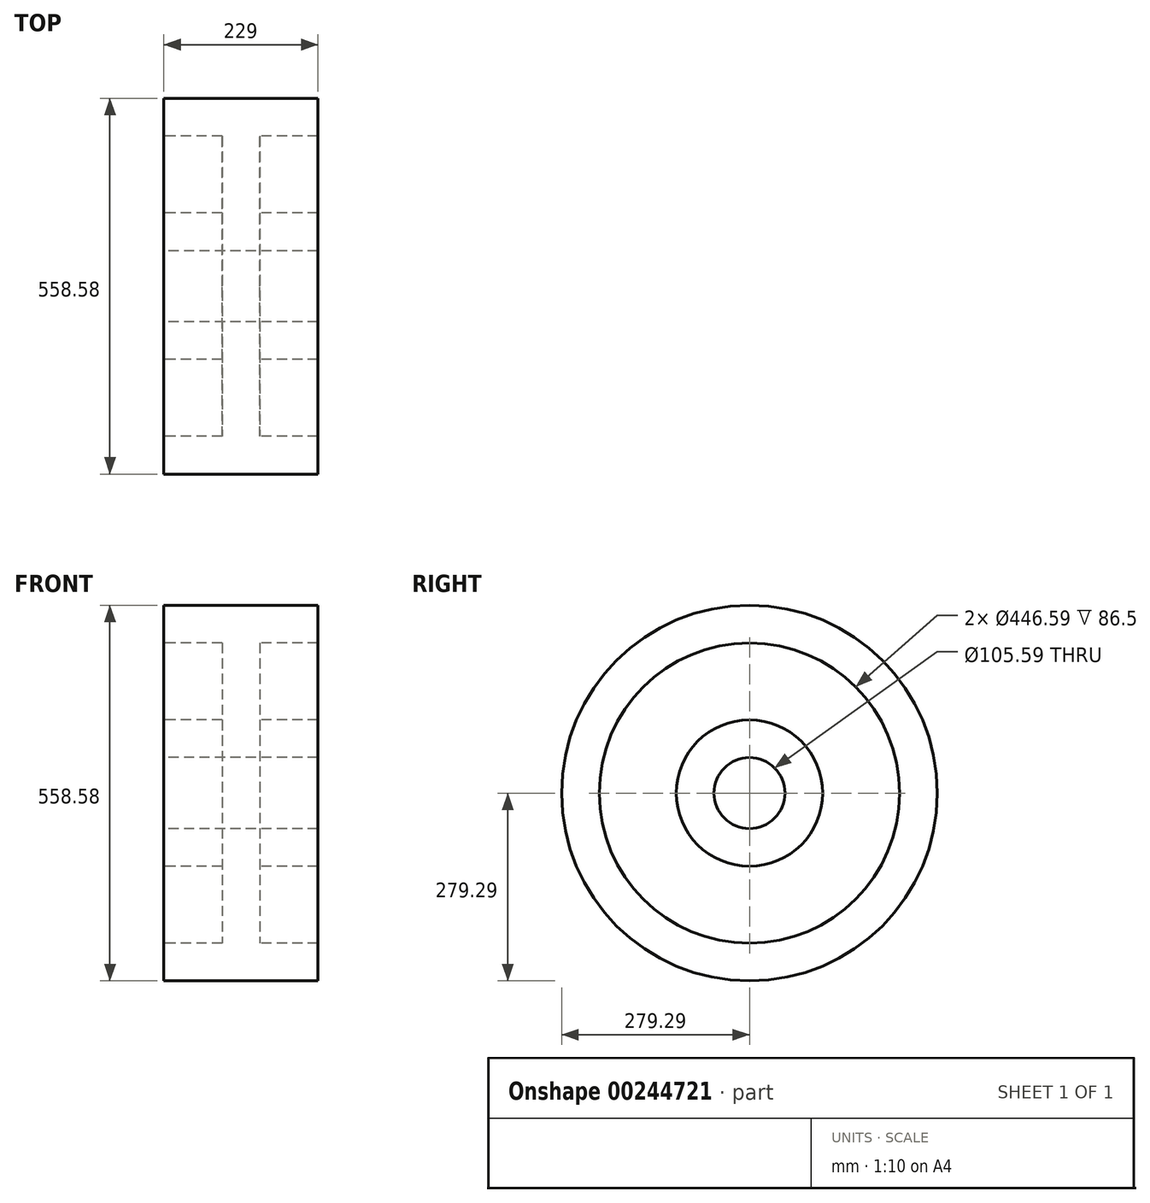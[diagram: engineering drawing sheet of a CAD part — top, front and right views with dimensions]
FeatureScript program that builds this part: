
annotation { "Feature Type Name" : "Feature", "Feature Type Description" : "" }
export const myFeature = defineFeature(function(context is Context, id is Id, definition is map)
    precondition{}
    {
        {
            var Q0;
            Q0=qCreatedBy(makeId("Front.planeOp"),FACE);
            var sketch = newSketch(context, id + "F0", { "sketchPlane" : qUnion([Q0])});
            skLineSegment(sketch, "E0", {"start": v(-122.5, 0) * mm, "end": v(122.5, 0) * mm, "construction": true});
            skLineSegment(sketch, "E1", {"start": v(-114.5, 279.3) * mm, "end": v(-114.5, 223.3) * mm});
            skLineSegment(sketch, "E2", {"start": v(-114.5, 279.3) * mm, "end": v(114.5, 279.3) * mm});
            skLineSegment(sketch, "E3", {"start": v(114.5, 279.3) * mm, "end": v(114.5, 223.3) * mm});
            skLineSegment(sketch, "E4", {"start": v(-114.5, 223.3) * mm, "end": v(-28, 223.3) * mm});
            skLineSegment(sketch, "E5", {"start": v(-28, 223.3) * mm, "end": v(-28, 108.8) * mm});
            skLineSegment(sketch, "E6", {"start": v(-28, 108.8) * mm, "end": v(-114.5, 108.8) * mm});
            skLineSegment(sketch, "E7", {"start": v(-114.5, 108.8) * mm, "end": v(-114.5, 52.8) * mm});
            skLineSegment(sketch, "E8", {"start": v(-114.5, 52.8) * mm, "end": v(114.5, 52.8) * mm});
            skLineSegment(sketch, "E9", {"start": v(114.5, 52.8) * mm, "end": v(114.5, 108.8) * mm});
            skLineSegment(sketch, "E10", {"start": v(28, 108.8) * mm, "end": v(28, 223.3) * mm});
            skLineSegment(sketch, "E11", {"start": v(28, 108.8) * mm, "end": v(114.5, 108.8) * mm});
            skLineSegment(sketch, "E12", {"start": v(28, 223.3) * mm, "end": v(114.5, 223.3) * mm});
            skLineSegment(sketch, "E13", {"start": v(0, 0) * mm, "end": v(0, 292.3) * mm, "construction": true});
            skPoint(sketch, "E13.endSnap0", {"position": v(0, 0) * mm});
            skSolve(sketch);
        }
        {
            var Q0;
            Q0 = qSketchRegion(id + "F0", true);
            var Q1;
            Q1=sQuery(id+"F0.wireOp",EDGE,"E0");
            revolve(context, id + "F1", {"entities" : qUnion([Q0]), "axis" : qUnion([Q1]), "revolveType" : RevolveType.FULL});
        }
    });
